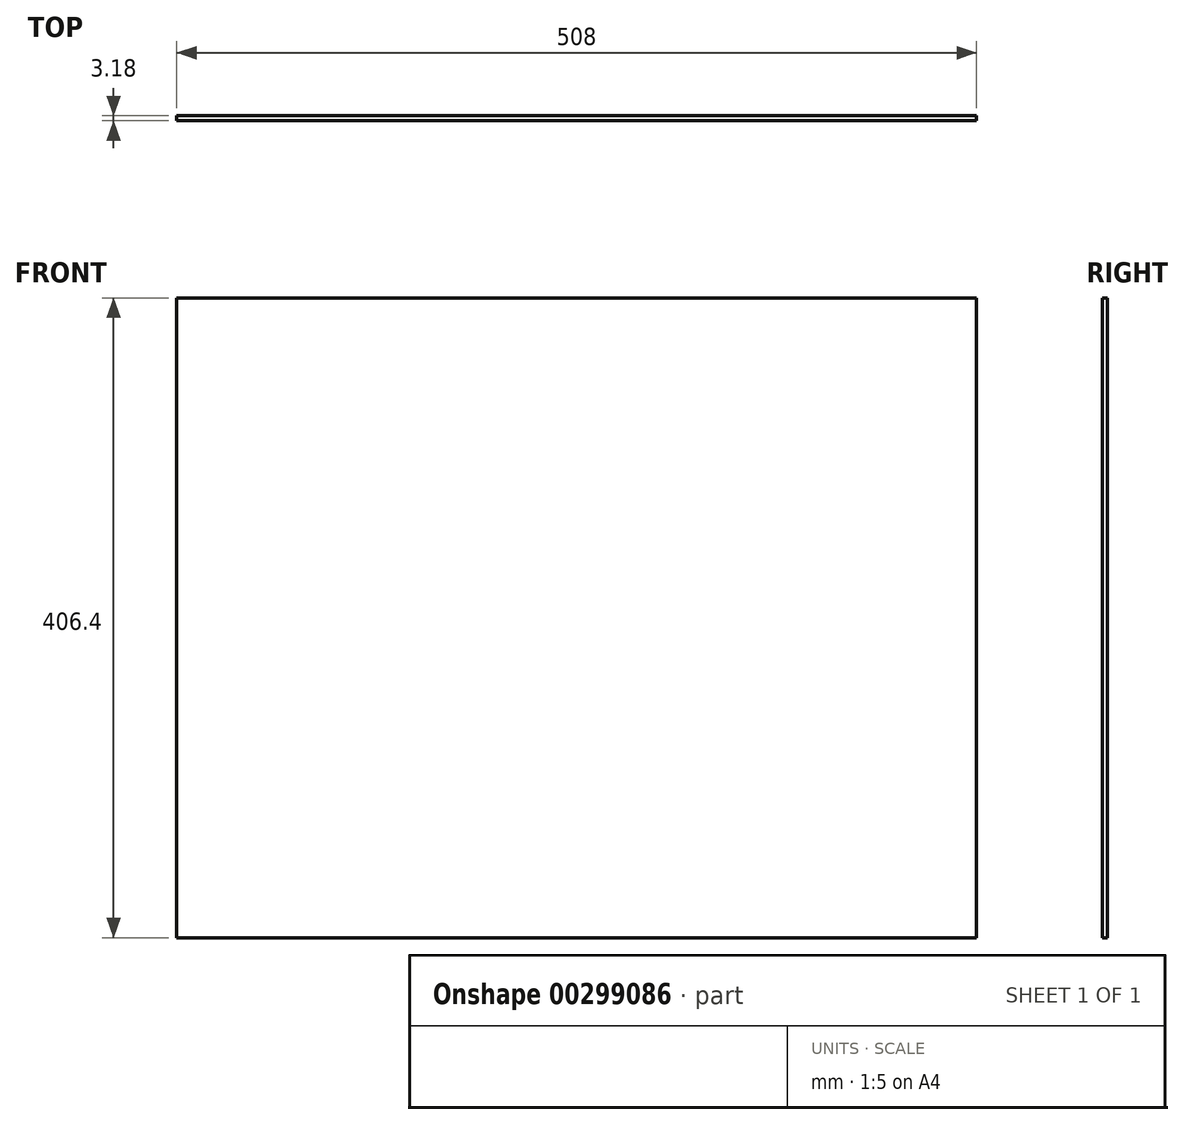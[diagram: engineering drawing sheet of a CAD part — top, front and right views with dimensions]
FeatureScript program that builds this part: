
annotation { "Feature Type Name" : "Feature", "Feature Type Description" : "" }
export const myFeature = defineFeature(function(context is Context, id is Id, definition is map)
    precondition{}
    {
        {
            var Q0;
            Q0=qCreatedBy(makeId("Front.planeOp"),FACE);
            var sketch = newSketch(context, id + "F0", { "sketchPlane" : qUnion([Q0])});
            skLineSegment(sketch, "E0.bottom", {"start": v(-254, 203.2) * mm, "end": v(254, 203.2) * mm});
            skLineSegment(sketch, "E0.top", {"start": v(-254, -203.2) * mm, "end": v(254, -203.2) * mm});
            skLineSegment(sketch, "E0.left", {"start": v(-254, 203.2) * mm, "end": v(-254, -203.2) * mm});
            skLineSegment(sketch, "E0.right", {"start": v(254, 203.2) * mm, "end": v(254, -203.2) * mm});
            skPoint(sketch, "E0.middle", {"position": v(0, 0) * mm});
            skLineSegment(sketch, "E1", {"start": v(0, 203.2) * mm, "end": v(127, 203.2) * mm});
            skLineSegment(sketch, "E2", {"start": v(0, 203.2) * mm, "end": v(-127, 203.2) * mm});
            skSolve(sketch);
        }
        {
            var Q0;
            Q0 = qSketchRegion(id + "F0", true);
            extrude(context, id + "F1", {"entities" : qUnion([Q0]), "endBound" : BoundingType.SYMMETRIC, "depth" : 3.17 * mm});
        }
    });
